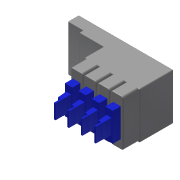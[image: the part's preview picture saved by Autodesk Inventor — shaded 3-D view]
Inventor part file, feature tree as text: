
AUTODESK INVENTOR PART (.ipt)
format: ipt  version: 2013 (Build 170138000, 138)  size: 303,104 bytes
history: native  units: in
note: dims shown in document units (in); Inventor stores cm internally (conversion verified against a paired STEP export)
features: extrude x7, sketch x7, fillet x2, pattern_linear x2
ambient origin geometry x8: Origin, YZ Plane, XZ Plane, XY Plane, X Axis, Y Axis, Z Axis, Center Point
bodies: Solid1 (feature_tree), Solid2 (feature_tree)
feature tree (18):
  extrude  "Extrusion1"  Depth=3.47in
  extrude  "Extrusion2"  Depth=4.11in
  extrude  "Extrusion3"  Depth=0.9in
  fillet  "Fillet1"  Radius=0.1in
  pattern_linear  "Rectangular Pattern1"  Count1=4 Spacing1=1.0in
  extrude  "Extrusion4"  Depth=0.293in TaperAngle=0.0deg
  fillet  "Fillet2"  Radius=0.0625in
  extrude  "Extrusion5"  Depth=0.563in
  extrude  "Extrusion7"  Depth=0.6in TaperAngle=0.0deg
  extrude  "Extrusion8"  Depth=1.15in
  pattern_linear  "Rectangular Pattern2"  Spacing1=0.375in  [1 undecoded]
  sketch  "Sketch1"  dims[d0=7.07in d1=3.47in]
  sketch  "Sketch2"  dims[d2=1.1in d3=0.0in d4=4.11in]
  sketch  "Sketch3"  dims[d6=1.431in d7=0.0in d8=0.9in d9=0.1in]
  sketch  "Sketch4"  dims[d10=1.128in d11=0.0in]
  sketch  "Sketch5"  dims[d12=0.125in d13=1.5748in d15=1.0in]
  sketch  "Sketch6"  dims[d16=1.14in d18=0.293in d19=0.0in d20=0.0625in]
  sketch  "Sketch7"  dims[d21=2.125in d23=0.563in d24=0.6in d25=0.0in d26=1.15in d28=0.375in d31=0.629in d32=-0.0206in d33=0.5in d34=0.0in d35=1.5748in d37=1.0in]
note: 1 required parameter value undecoded (feature->parameter linkage not recoverable at this tier; creation-order binding heuristic only, values carry confidence <= 0.55)
